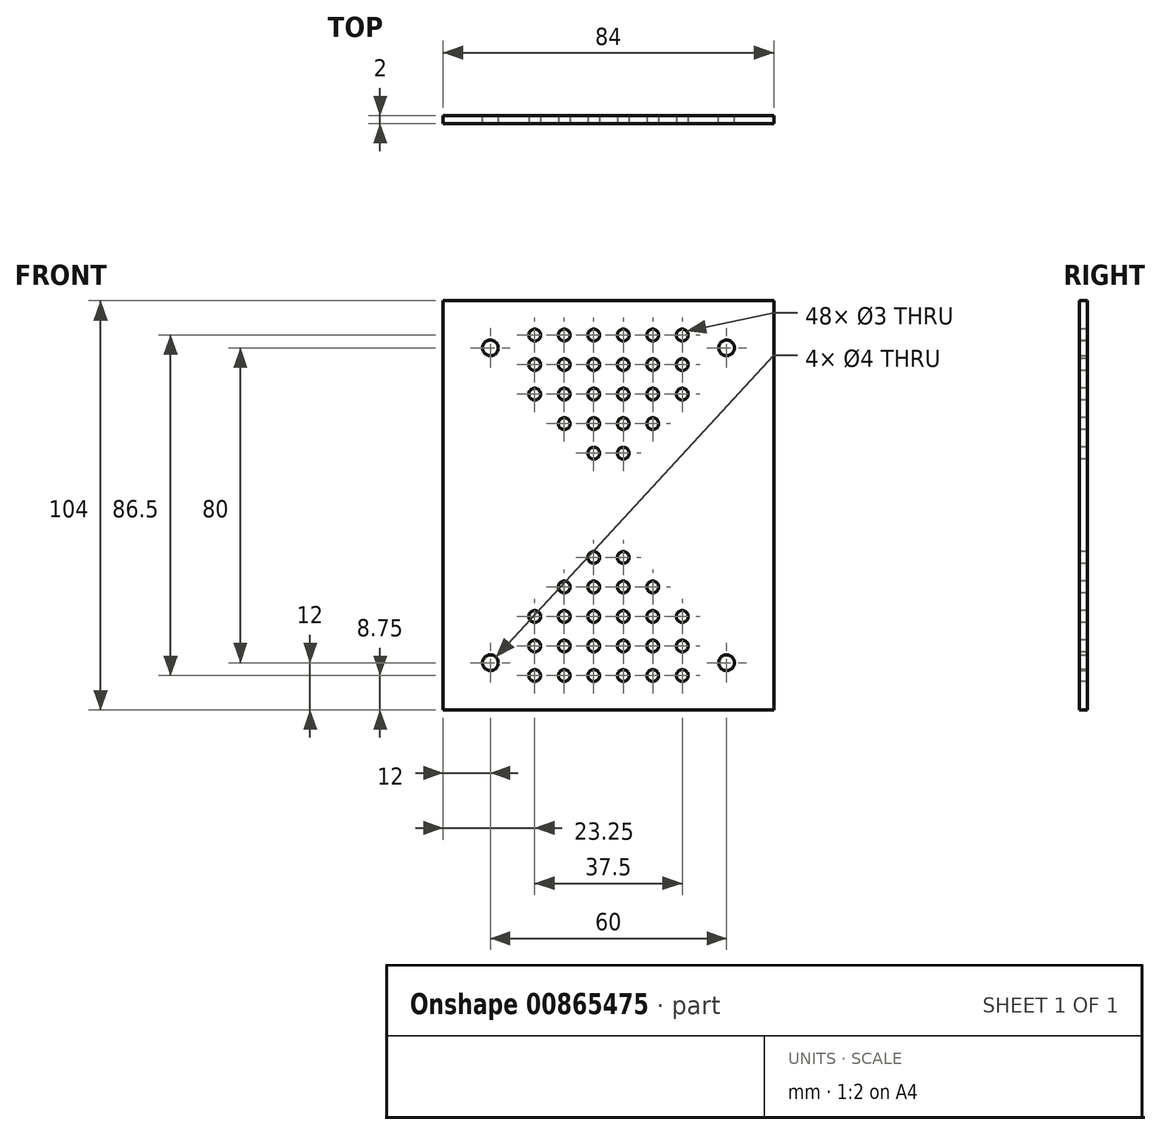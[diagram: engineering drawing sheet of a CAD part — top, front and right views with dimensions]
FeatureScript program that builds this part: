
annotation { "Feature Type Name" : "Feature", "Feature Type Description" : "" }
export const myFeature = defineFeature(function(context is Context, id is Id, definition is map)
    precondition{}
    {
        {
            var Q0;
            Q0=qCreatedBy(makeId("Front.planeOp"),FACE);
            var sketch = newSketch(context, id + "F0", { "sketchPlane" : qUnion([Q0])});
            skLineSegment(sketch, "E0.bottom", {"start": v(42, 52) * mm, "end": v(-42, 52) * mm});
            skLineSegment(sketch, "E0.top", {"start": v(42, -52) * mm, "end": v(-42, -52) * mm});
            skLineSegment(sketch, "E0.left", {"start": v(42, 52) * mm, "end": v(42, -52) * mm});
            skLineSegment(sketch, "E0.right", {"start": v(-42, 52) * mm, "end": v(-42, -52) * mm});
            skPoint(sketch, "E0.middle", {"position": v(0, 0) * mm});
            skCircle(sketch, "E1", {"center": v(-30, 40) * mm, "radius": 2 * mm});
            skCircle(sketch, "E2", {"center": v(30, 40) * mm, "radius": 2 * mm});
            skCircle(sketch, "E3", {"center": v(30, -40) * mm, "radius": 2 * mm});
            skCircle(sketch, "E4", {"center": v(-30, -40) * mm, "radius": 2 * mm});
            skSolve(sketch);
        }
        {
            var Q0;
            Q0=qSketchRegion(id+"F0",true);
            extrude(context, id + "F1", {"entities" : qUnion([Q0]), "depth" : 2 * mm, "offsetDistance" : 25 * mm});
        }
        {
            var Q0;
            Q0=makeQuery(id+"F1.opExtrude","CAP_FACE",FACE,{"disambiguationData":[OSD([sQuery(id+"F0.wireOp",EDGE,"E0.bottom"),sQuery(id+"F0.wireOp",EDGE,"E0.top"),sQuery(id+"F0.wireOp",EDGE,"E0.left"),sQuery(id+"F0.wireOp",EDGE,"E0.right"),sQuery(id+"F0.wireOp",EDGE,"E1"),sQuery(id+"F0.wireOp",EDGE,"E2"),sQuery(id+"F0.wireOp",EDGE,"E3"),sQuery(id+"F0.wireOp",EDGE,"E4")])],"isStart":false});
            var sketch = newSketch(context, id + "F2", { "sketchPlane" : qUnion([Q0])});
            skCircle(sketch, "E5", {"center": v(-3.75, 43.25) * mm, "radius": 1.5 * mm});
            skCircle(sketch, "E6.0.1.0", {"center": v(-3.75, 35.75) * mm, "radius": 1.5 * mm});
            skCircle(sketch, "E6.0.2.0", {"center": v(-3.75, 28.25) * mm, "radius": 1.5 * mm});
            skCircle(sketch, "E6.0.3.0", {"center": v(-3.75, 20.75) * mm, "radius": 1.5 * mm});
            skCircle(sketch, "E6.0.4.0", {"center": v(-3.75, 13.25) * mm, "radius": 1.5 * mm});
            skCircle(sketch, "E6.1.0.0", {"center": v(-11.25, 43.25) * mm, "radius": 1.5 * mm});
            skCircle(sketch, "E6.1.1.0", {"center": v(-11.25, 35.75) * mm, "radius": 1.5 * mm});
            skCircle(sketch, "E6.1.2.0", {"center": v(-11.25, 28.25) * mm, "radius": 1.5 * mm});
            skCircle(sketch, "E6.1.3.0", {"center": v(-11.25, 20.75) * mm, "radius": 1.5 * mm});
            skCircle(sketch, "E6.2.0.0", {"center": v(-18.75, 43.25) * mm, "radius": 1.5 * mm});
            skCircle(sketch, "E6.2.1.0", {"center": v(-18.75, 35.75) * mm, "radius": 1.5 * mm});
            skCircle(sketch, "E6.2.2.0", {"center": v(-18.75, 28.25) * mm, "radius": 1.5 * mm});
            skLineSegment(sketch, "E6.direction1", {"start": v(-3.75, 43.25) * mm, "end": v(-11.25, 43.25) * mm, "construction": true});
            skLineSegment(sketch, "E6.direction2", {"start": v(-3.75, 43.25) * mm, "end": v(-3.75, 35.75) * mm, "construction": true});
            skCircle(sketch, "E7.MirrorC", {"center": v(11.25, 43.25) * mm, "radius": 1.5 * mm});
            skCircle(sketch, "E8.MirrorC", {"center": v(3.75, 13.25) * mm, "radius": 1.5 * mm});
            skCircle(sketch, "E9.MirrorC", {"center": v(11.25, 35.75) * mm, "radius": 1.5 * mm});
            skCircle(sketch, "E10.MirrorC", {"center": v(11.25, 28.25) * mm, "radius": 1.5 * mm});
            skCircle(sketch, "E11.MirrorC", {"center": v(11.25, 20.75) * mm, "radius": 1.5 * mm});
            skCircle(sketch, "E12.MirrorC", {"center": v(18.75, 43.25) * mm, "radius": 1.5 * mm});
            skCircle(sketch, "E13.MirrorC", {"center": v(18.75, 35.75) * mm, "radius": 1.5 * mm});
            skCircle(sketch, "E14.MirrorC", {"center": v(18.75, 28.25) * mm, "radius": 1.5 * mm});
            skLineSegment(sketch, "E15.MirrorCS", {"start": v(3.75, 43.25) * mm, "end": v(11.25, 43.25) * mm, "construction": true});
            skLineSegment(sketch, "E16.MirrorCS", {"start": v(3.75, 43.25) * mm, "end": v(3.75, 35.75) * mm, "construction": true});
            skCircle(sketch, "E17.MirrorC", {"center": v(3.75, 43.25) * mm, "radius": 1.5 * mm});
            skCircle(sketch, "E18.MirrorC", {"center": v(3.75, 35.75) * mm, "radius": 1.5 * mm});
            skCircle(sketch, "E19.MirrorC", {"center": v(3.75, 28.25) * mm, "radius": 1.5 * mm});
            skCircle(sketch, "E20.MirrorC", {"center": v(3.75, 20.75) * mm, "radius": 1.5 * mm});
            skCircle(sketch, "E21.MirrorC", {"center": v(-3.75, -43.25) * mm, "radius": 1.5 * mm});
            skCircle(sketch, "E22.MirrorC", {"center": v(-11.25, -43.25) * mm, "radius": 1.5 * mm});
            skCircle(sketch, "E23.MirrorC", {"center": v(3.75, -28.25) * mm, "radius": 1.5 * mm});
            skCircle(sketch, "E24.MirrorC", {"center": v(-3.75, -20.75) * mm, "radius": 1.5 * mm});
            skCircle(sketch, "E25.MirrorC", {"center": v(-11.25, -28.25) * mm, "radius": 1.5 * mm});
            skCircle(sketch, "E26.MirrorC", {"center": v(-3.75, -28.25) * mm, "radius": 1.5 * mm});
            skCircle(sketch, "E27.MirrorC", {"center": v(18.75, -43.25) * mm, "radius": 1.5 * mm});
            skCircle(sketch, "E28.MirrorC", {"center": v(11.25, -28.25) * mm, "radius": 1.5 * mm});
            skCircle(sketch, "E29.MirrorC", {"center": v(-18.75, -28.25) * mm, "radius": 1.5 * mm});
            skCircle(sketch, "E30.MirrorC", {"center": v(11.25, -35.75) * mm, "radius": 1.5 * mm});
            skCircle(sketch, "E31.MirrorC", {"center": v(-3.75, -35.75) * mm, "radius": 1.5 * mm});
            skCircle(sketch, "E32.MirrorC", {"center": v(3.75, -20.75) * mm, "radius": 1.5 * mm});
            skCircle(sketch, "E33.MirrorC", {"center": v(18.75, -35.75) * mm, "radius": 1.5 * mm});
            skCircle(sketch, "E34.MirrorC", {"center": v(-18.75, -35.75) * mm, "radius": 1.5 * mm});
            skCircle(sketch, "E35.MirrorC", {"center": v(3.75, -35.75) * mm, "radius": 1.5 * mm});
            skCircle(sketch, "E36.MirrorC", {"center": v(11.25, -43.25) * mm, "radius": 1.5 * mm});
            skCircle(sketch, "E37.MirrorC", {"center": v(3.75, -13.25) * mm, "radius": 1.5 * mm});
            skCircle(sketch, "E38.MirrorC", {"center": v(-11.25, -35.75) * mm, "radius": 1.5 * mm});
            skLineSegment(sketch, "E39.MirrorCS", {"start": v(3.75, -43.25) * mm, "end": v(3.75, -35.75) * mm, "construction": true});
            skCircle(sketch, "E40.MirrorC", {"center": v(-3.75, -13.25) * mm, "radius": 1.5 * mm});
            skCircle(sketch, "E41.MirrorC", {"center": v(18.75, -28.25) * mm, "radius": 1.5 * mm});
            skCircle(sketch, "E42.MirrorC", {"center": v(-11.25, -20.75) * mm, "radius": 1.5 * mm});
            skCircle(sketch, "E43.MirrorC", {"center": v(11.25, -20.75) * mm, "radius": 1.5 * mm});
            skCircle(sketch, "E44.MirrorC", {"center": v(-18.75, -43.25) * mm, "radius": 1.5 * mm});
            skLineSegment(sketch, "E45.MirrorCS", {"start": v(-3.75, -43.25) * mm, "end": v(-11.25, -43.25) * mm, "construction": true});
            skLineSegment(sketch, "E46.MirrorCS", {"start": v(-3.75, -43.25) * mm, "end": v(-3.75, -35.75) * mm, "construction": true});
            skCircle(sketch, "E47.MirrorC", {"center": v(3.75, -43.25) * mm, "radius": 1.5 * mm});
            skLineSegment(sketch, "E48.MirrorCS", {"start": v(3.75, -43.25) * mm, "end": v(11.25, -43.25) * mm, "construction": true});
            skSolve(sketch);
        }
        {
            var Q0;
            Q0 = qSketchRegion(id + "F2", true);
            extrude(context, id + "F3", {"entities" : qUnion([Q0]), "operationType" : NewBodyOperationType.REMOVE, "endBound" : BoundingType.THROUGH_ALL, "oppositeDirection" : true, "depth" : 25 * mm, "offsetDistance" : 25 * mm});
        }
    });
